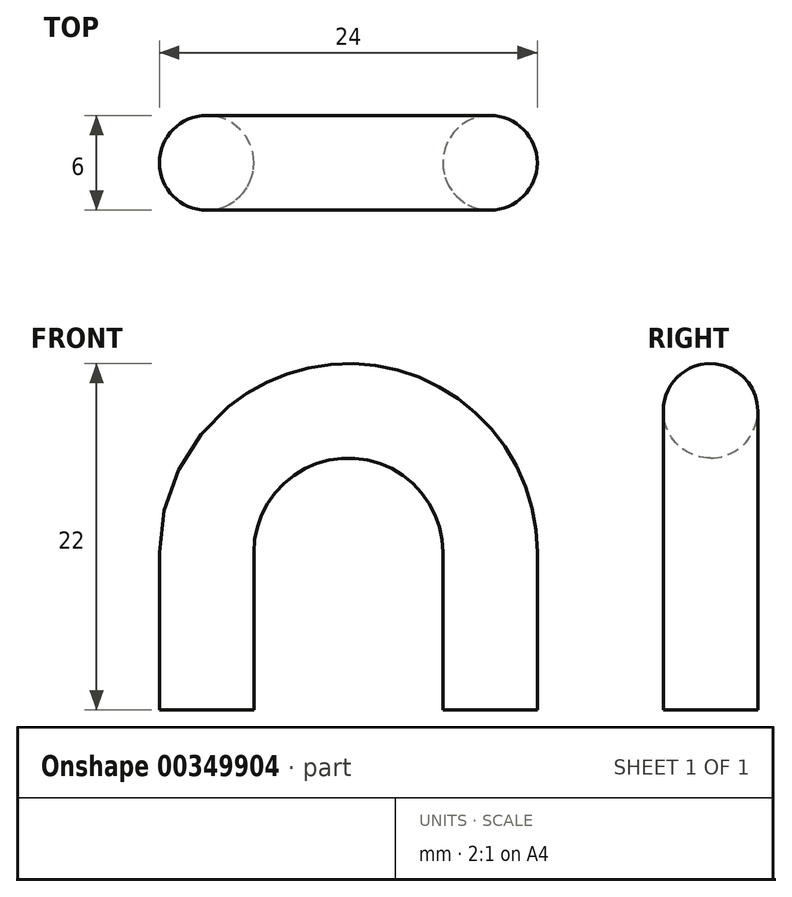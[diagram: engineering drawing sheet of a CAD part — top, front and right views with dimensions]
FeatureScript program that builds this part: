
annotation { "Feature Type Name" : "Feature", "Feature Type Description" : "" }
export const myFeature = defineFeature(function(context is Context, id is Id, definition is map)
    precondition{}
    {
        {
            var Q0;
            Q0=qCreatedBy(makeId("Top.planeOp"),FACE);
            var sketch = newSketch(context, id + "F0", { "sketchPlane" : qUnion([Q0])});
            skCircle(sketch, "E0", {"center": v(-9, 0) * mm, "radius": 3 * mm});
            skCircle(sketch, "E1.MirrorC", {"center": v(9, 0) * mm, "radius": 3 * mm});
            skSolve(sketch);
        }
        {
            var Q0;
            Q0=qCreatedBy(makeId("Front.planeOp"),FACE);
            var sketch = newSketch(context, id + "F1", { "sketchPlane" : qUnion([Q0])});
            skLineSegment(sketch, "E2", {"start": v(-9, 0) * mm, "end": v(-9, 10) * mm});
            skLineSegment(sketch, "E3.MirrorCS", {"start": v(9, 0) * mm, "end": v(9, 10) * mm});
            skArc(sketch, "E4", {"start": v(9, 10) * mm, "mid": v(0, 19) * mm, "end": v(-9, 10) * mm});
            skSolve(sketch);
        }
        {
            var Q0;
            Q0=makeQuery(id+"F0.imprint","IMPRINT",FACE,{"disambiguationData":[TD([[makeQuery(id+"F0.imprint","IMPRINT",EDGE,{"derivedFrom":sQuery(id+"F0.wireOp",EDGE,"E0")}),1.0]])]});
            var Q1;
            Q1=sQuery(id+"F1.wireOp",EDGE,"E2");
            var Q2;
            Q2=sQuery(id+"F1.wireOp",EDGE,"E4");
            var Q3;
            Q3=sQuery(id+"F1.wireOp",EDGE,"E3.MirrorCS");
            sweep(context, id + "F2", {"profiles" : qUnion([Q0]), "path" : qUnion([Q1, Q2, Q3])});
        }
    });
